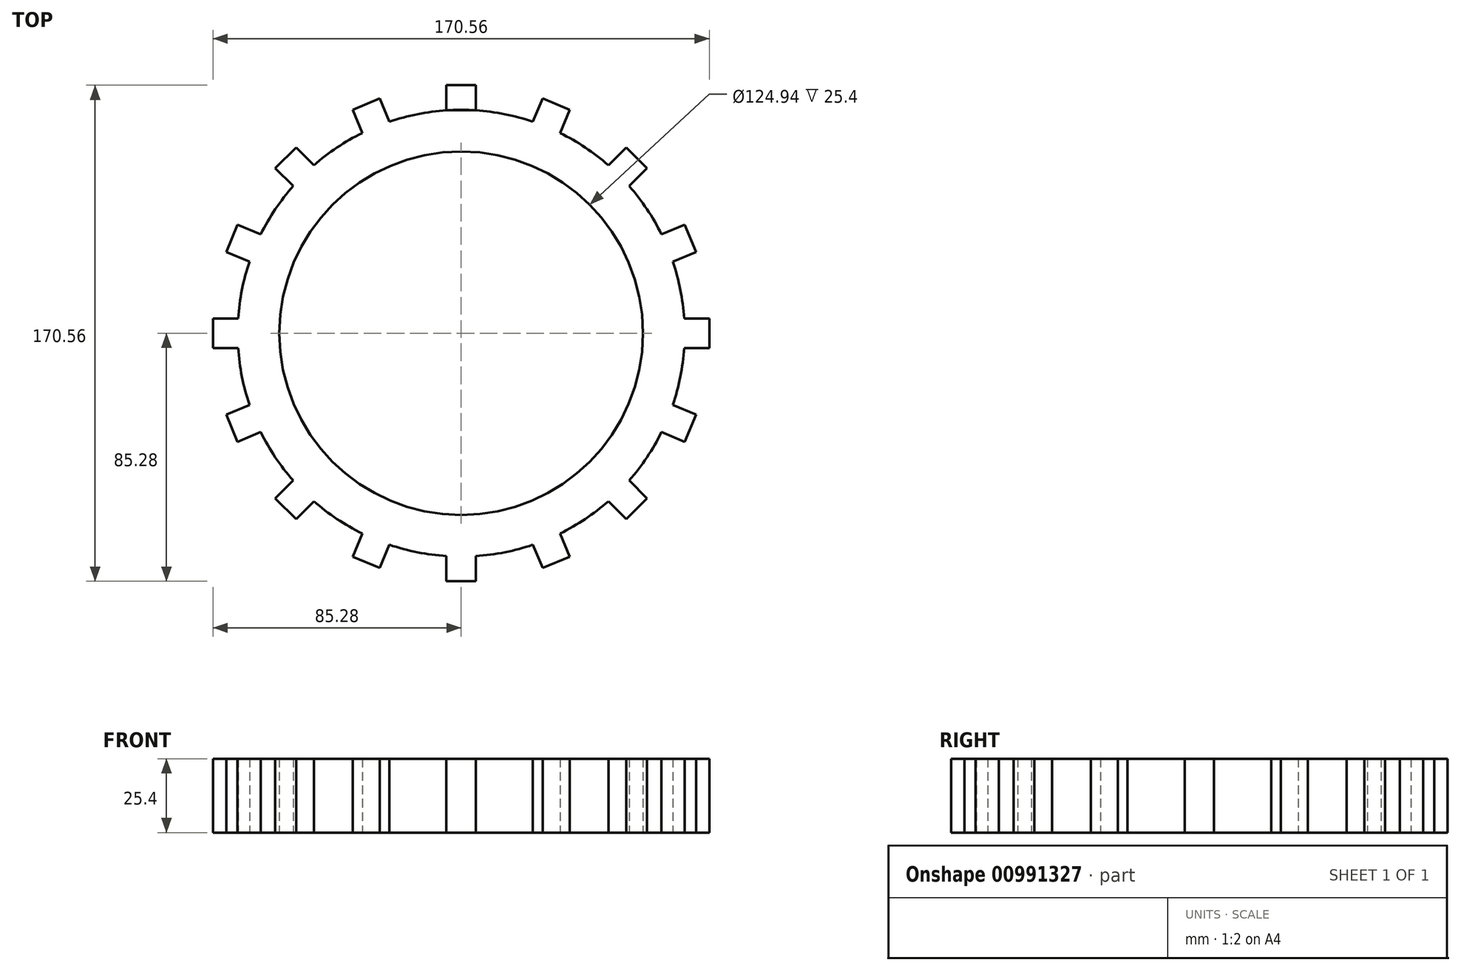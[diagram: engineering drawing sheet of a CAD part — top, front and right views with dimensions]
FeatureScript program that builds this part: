
annotation { "Feature Type Name" : "Feature", "Feature Type Description" : "" }
export const myFeature = defineFeature(function(context is Context, id is Id, definition is map)
    precondition{}
    {
        {
            var Q0;
            Q0=qCreatedBy(makeId("Top.planeOp"),FACE);
            var sketch = newSketch(context, id + "F0", { "sketchPlane" : qUnion([Q0])});
            skCircle(sketch, "E0", {"center": v(0, 0) * mm, "radius": 76.8 * mm});
            skLineSegment(sketch, "E1", {"start": v(0, 0) * mm, "end": v(0, 76.8) * mm});
            skLineSegment(sketch, "E2.bottom", {"start": v(5.05, 76.63) * mm, "end": v(-5.05, 76.63) * mm});
            skLineSegment(sketch, "E2.left", {"start": v(5.05, 76.63) * mm, "end": v(5.05, 85.28) * mm});
            skLineSegment(sketch, "E2.right", {"start": v(-5.05, 76.63) * mm, "end": v(-5.05, 85.28) * mm});
            skPoint(sketch, "E2.middle", {"position": v(0, 85.28) * mm});
            skLineSegment(sketch, "E3", {"start": v(0, 85.28) * mm, "end": v(5.05, 85.28) * mm});
            skLineSegment(sketch, "E4", {"start": v(5.05, 85.28) * mm, "end": v(-5.05, 85.28) * mm});
            skPoint(sketch, "E4.endSnap0", {"position": v(-5.05, 85.28) * mm});
            skPoint(sketch, "E5.orphan", {"position": v(-12.25, 85.28) * mm});
            skPoint(sketch, "E6.orphan", {"position": v(-5.05, 93.94) * mm});
            skPoint(sketch, "E7.orphan", {"position": v(5.05, 93.94) * mm});
            skCircle(sketch, "E8", {"center": v(0, 0) * mm, "radius": 62.47 * mm});
            skSolve(sketch);
        }
        {
            var Q0;
            {var subQ1=sQuery(id+"F0.wireOp",EDGE,"E2.left");Q0=makeQuery(id+"F0.imprint","IMPRINT",FACE,{"disambiguationData":[TD([[makeQuery(id+"F0.imprint","IMPRINT",EDGE,{"derivedFrom":subQ1}),1.0]])]});}
            extrude(context, id + "F1", {"entities" : qUnion([Q0]), "depth" : 25.4 * mm, "offsetDistance" : 25.4 * mm});
        }
        {
            var Q0;
            Q0=makeQuery(id+"F1.opExtrude","SWEPT_BODY",BODY,{"disambiguationData":[OSD([sQuery(id+"F0.wireOp",EDGE,"E0"),sQuery(id+"F0.wireOp",EDGE,"E2.left"),sQuery(id+"F0.wireOp",EDGE,"E2.right"),sQuery(id+"F0.wireOp",EDGE,"E4")])]});
            var Q1;
            Q1=sQuery(id+"F0.wireOp",EDGE,"E0");
            circularPattern(context, id + "F2", {"entities" : qUnion([Q0]), "axis" : qUnion([Q1]), "angle" : 360 * degree, "instanceCount" : 16, "equalSpace" : true});
        }
        {
            var Q0;
            Q0=makeQuery(id+"F0.imprint","IMPRINT",FACE,{"disambiguationData":[TD([[makeQuery(id+"F0.imprint","IMPRINT",EDGE,{"derivedFrom":sQuery(id+"F0.wireOp",EDGE,"E8")}),-1.0]])]});
            extrude(context, id + "F3", {"entities" : qUnion([Q0]), "operationType" : NewBodyOperationType.ADD, "depth" : 25.4 * mm, "offsetDistance" : 25.4 * mm});
        }
    });
